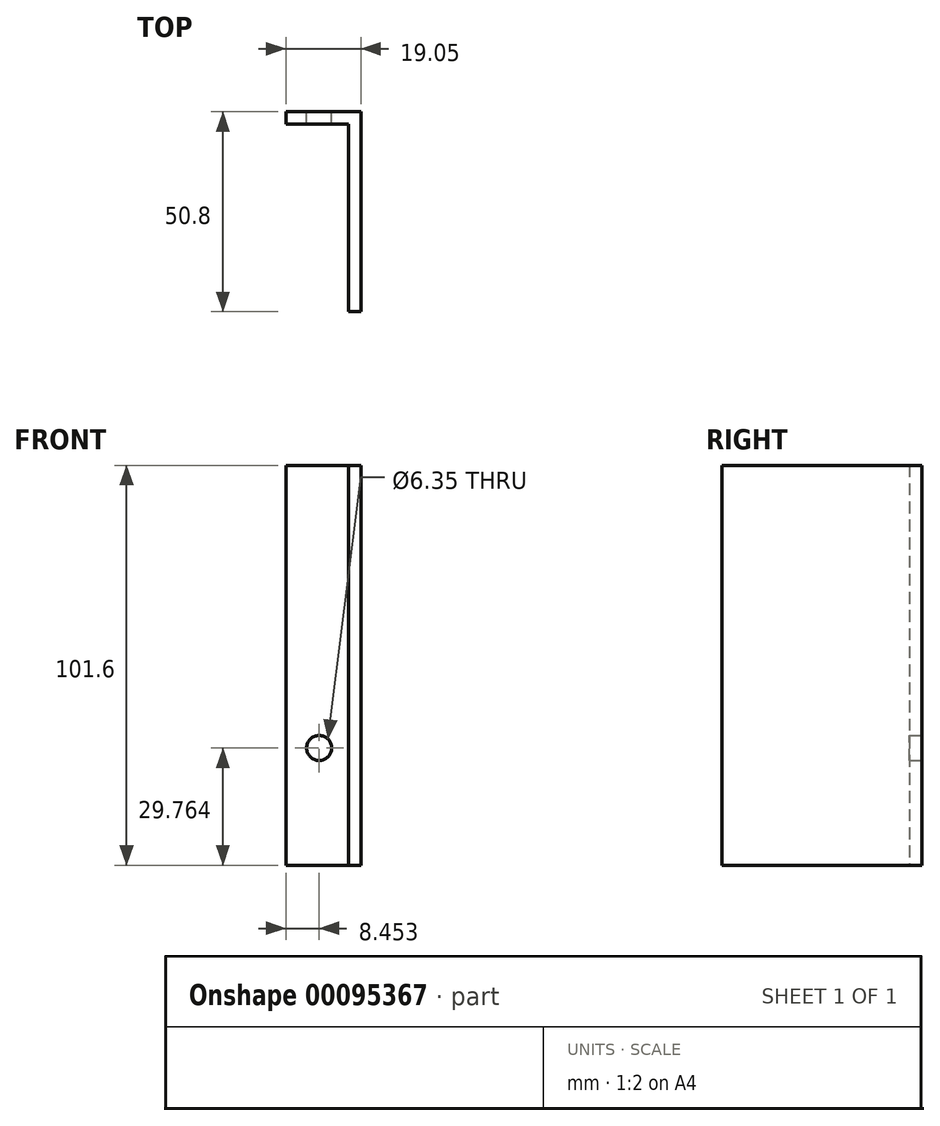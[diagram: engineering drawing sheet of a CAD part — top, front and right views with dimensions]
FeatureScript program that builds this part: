
annotation { "Feature Type Name" : "Feature", "Feature Type Description" : "" }
export const myFeature = defineFeature(function(context is Context, id is Id, definition is map)
    precondition{}
    {
        {
            var Q0;
            Q0=qCreatedBy(makeId("Top.planeOp"),FACE);
            var sketch = newSketch(context, id + "F0", { "sketchPlane" : qUnion([Q0])});
            skLineSegment(sketch, "E0", {"start": v(-19.05, 0) * mm, "end": v(0, 0) * mm});
            skLineSegment(sketch, "E1", {"start": v(0, 0) * mm, "end": v(0, -50.8) * mm});
            skLineSegment(sketch, "E2", {"start": v(0, -50.8) * mm, "end": v(-3.18, -50.8) * mm});
            skLineSegment(sketch, "E3", {"start": v(-3.18, -50.8) * mm, "end": v(-3.18, -3.18) * mm});
            skLineSegment(sketch, "E4", {"start": v(-3.18, -3.17) * mm, "end": v(-19.05, -3.18) * mm});
            skLineSegment(sketch, "E5", {"start": v(-19.05, -3.18) * mm, "end": v(-19.05, 0) * mm});
            skSolve(sketch);
        }
        {
            var Q0;
            Q0=makeQuery(id+"F0.imprint","IMPRINT",FACE,{"disambiguationData":[TD([[makeQuery(id+"F0.imprint","IMPRINT",EDGE,{"derivedFrom":sQuery(id+"F0.wireOp",EDGE,"E0")}),-1.0]])]});
            extrude(context, id + "F1", {"entities" : qUnion([Q0]), "depth" : 101.6 * mm});
        }
        {
            var Q0;
            Q0=qCreatedBy(makeId("Front.planeOp"),FACE);
            var sketch = newSketch(context, id + "F2", { "sketchPlane" : qUnion([Q0])});
            skLineSegment(sketch, "E6", {"start": v(-10.6, 0) * mm, "end": v(-10.6, 101.64) * mm, "construction": true});
            skPoint(sketch, "E7", {"position": v(-10.6, 29.76) * mm});
            skLineSegment(sketch, "E8", {"start": v(-3.76, 101.52) * mm, "end": v(-19.78, 81.75) * mm});
            skSolve(sketch);
        }
        {
            var Q0;
            Q0=sQuery(id+"F2.wireOp",VERTEX,"E7");
            var Q1;
            Q1=makeQuery(id+"F1.opExtrude","SWEPT_BODY",BODY,{"disambiguationData":[OSD([sQuery(id+"F0.wireOp",EDGE,"E0"),sQuery(id+"F0.wireOp",EDGE,"E1"),sQuery(id+"F0.wireOp",EDGE,"E2"),sQuery(id+"F0.wireOp",EDGE,"E3"),sQuery(id+"F0.wireOp",EDGE,"E4"),sQuery(id+"F0.wireOp",EDGE,"E5")])]});
            hole(context, id + "F3", {"style" : HoleStyle.SIMPLE, "endStyle" : HoleEndStyle.THROUGH, "oppositeDirection" : true, "holeDiameter" : 6.35 * mm, "locations" : qUnion([Q0]), "scope" : qUnion([Q1]), "isTappedThrough" : true});
        }
    });
